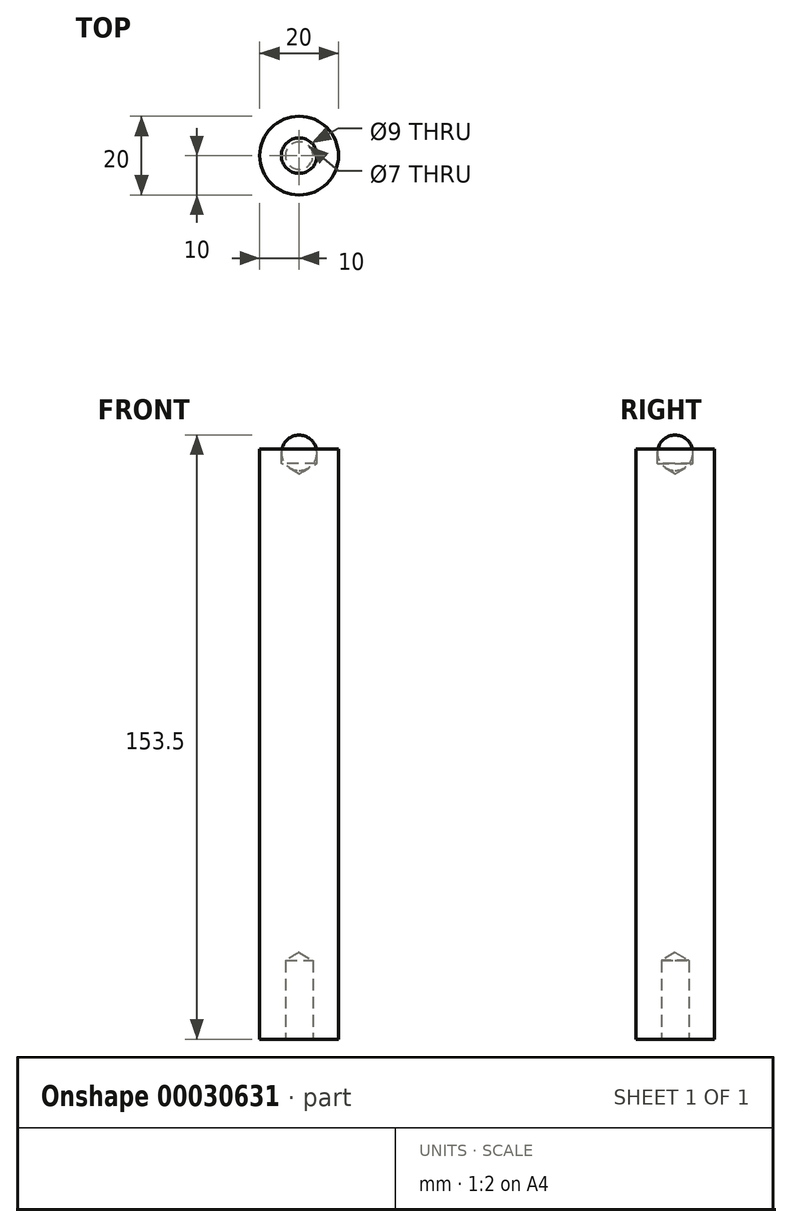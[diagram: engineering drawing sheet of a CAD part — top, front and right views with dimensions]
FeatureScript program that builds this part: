
annotation { "Feature Type Name" : "Feature", "Feature Type Description" : "" }
export const myFeature = defineFeature(function(context is Context, id is Id, definition is map)
    precondition{}
    {
        {
            var Q0;
            Q0=qCreatedBy(makeId("Front.planeOp"),FACE);
            var sketch = newSketch(context, id + "F0", { "sketchPlane" : qUnion([Q0])});
            skLineSegment(sketch, "E0.0", {"start": v(-10, 150) * mm, "end": v(-10, 0) * mm});
            skLineSegment(sketch, "E1", {"start": v(-10, 0) * mm, "end": v(0, 0) * mm});
            skLineSegment(sketch, "E2.0", {"start": v(-10, 150) * mm, "end": v(0, 150) * mm});
            skPoint(sketch, "E3.orphan", {"position": v(0, 44.07) * mm});
            skLineSegment(sketch, "E4", {"start": v(0, 150) * mm, "end": v(0, 0) * mm});
            skLineSegment(sketch, "E5", {"start": v(0, 150) * mm, "end": v(0, -57.25) * mm, "construction": true});
            skSolve(sketch);
        }
        {
            var Q0;
            Q0=makeQuery(id+"F0.imprint","IMPRINT",FACE,{"disambiguationData":[TD([[makeQuery(id+"F0.imprint","IMPRINT",EDGE,{"derivedFrom":sQuery(id+"F0.wireOp",EDGE,"E0.0")}),1.0]])]});
            var Q1;
            Q1=sQuery(id+"F0.wireOp",EDGE,"E5");
            revolve(context, id + "F1", {"entities" : qUnion([Q0]), "axis" : qUnion([Q1]), "revolveType" : RevolveType.FULL});
        }
        {
            var Q0;
            Q0=makeQuery(id+"F1.opRevolve","SWEPT_FACE",FACE,{"disambiguationData":[OSD([sQuery(id+"F0.wireOp",EDGE,"E2.0")])]});
            var sketch = newSketch(context, id + "F2", { "sketchPlane" : qUnion([Q0])});
            skCircle(sketch, "E6.0", {"center": v(0, 0) * mm, "radius": 10 * mm});
            skSolve(sketch);
        }
        {
            var Q0;
            Q0=sQuery(id+"F2.wireOp",VERTEX,"E6.0.center");
            var Q1;
            Q1=makeQuery(id+"F1.opRevolve","SWEPT_BODY",BODY,{"disambiguationData":[OSD([sQuery(id+"F0.wireOp",EDGE,"E0.0"),sQuery(id+"F0.wireOp",EDGE,"E1"),sQuery(id+"F0.wireOp",EDGE,"E2.0"),sQuery(id+"F0.wireOp",EDGE,"E4")])]});
            hole(context, id + "F3", {"style" : HoleStyle.SIMPLE, "holeDiameter" : 9 * mm, "endStyle" : HoleEndStyle.BLIND, "holeDepth" : 3.7 * mm, "locations" : qUnion([Q0]), "scope" : qUnion([Q1])});
        }
        {
            var Q0;
            Q0=makeQuery(id+"F1.opRevolve","SWEPT_FACE",FACE,{"disambiguationData":[OSD([sQuery(id+"F0.wireOp",EDGE,"E1")])]});
            var sketch = newSketch(context, id + "F4", { "sketchPlane" : qUnion([Q0])});
            skCircle(sketch, "E7.0", {"center": v(0, 0) * mm, "radius": 10 * mm});
            skSolve(sketch);
        }
        {
            var Q0;
            Q0=sQuery(id+"F4.wireOp",VERTEX,"E7.0.center");
            var Q1;
            Q1=makeQuery(id+"F1.opRevolve","SWEPT_BODY",BODY,{"disambiguationData":[OSD([sQuery(id+"F0.wireOp",EDGE,"E0.0"),sQuery(id+"F0.wireOp",EDGE,"E1"),sQuery(id+"F0.wireOp",EDGE,"E2.0"),sQuery(id+"F0.wireOp",EDGE,"E4")])]});
            hole(context, id + "F5", {"style" : HoleStyle.SIMPLE, "holeDiameter" : 7 * mm, "endStyle" : HoleEndStyle.BLIND, "holeDepth" : 20 * mm, "locations" : qUnion([Q0]), "scope" : qUnion([Q1])});
        }
        {
            var Q0;
            Q0=qCreatedBy(makeId("Front.planeOp"),FACE);
            var sketch = newSketch(context, id + "F6", { "sketchPlane" : qUnion([Q0])});
            skLineSegment(sketch, "E8.0", {"start": v(-4.5, 146.3) * mm, "end": v(4.5, 146.3) * mm, "construction": true});
            skLineSegment(sketch, "E9", {"start": v(4.5, 150) * mm, "end": v(4.5, 146) * mm});
            skLineSegment(sketch, "E10", {"start": v(-4.5, 146) * mm, "end": v(-4.5, 150) * mm});
            skLineSegment(sketch, "E11.0", {"start": v(-4.5, 150) * mm, "end": v(4.5, 150) * mm, "construction": true});
            skLineSegment(sketch, "E12", {"start": v(0, 144.5) * mm, "end": v(0, 153.74) * mm, "construction": true});
            skLineSegment(sketch, "E13.0", {"start": v(-3.5, 149) * mm, "end": v(3.5, 149) * mm, "construction": true});
            skArc(sketch, "E14", {"start": v(0, 153.5) * mm, "mid": v(-4.5, 149) * mm, "end": v(0, 144.5) * mm});
            skPoint(sketch, "E15.orphan", {"position": v(0, 146.3) * mm});
            skLineSegment(sketch, "E16", {"start": v(0, 144.5) * mm, "end": v(0, 153.5) * mm});
            skSolve(sketch);
        }
        {
            var Q0;
            {var subQ0=sQuery(id+"F6.wireOp",EDGE,"E16");Q0=makeQuery(id+"F6.imprint","IMPRINT",FACE,{"disambiguationData":[TD([[makeQuery(id+"F6.imprint","IMPRINT",EDGE,{"derivedFrom":subQ0}),1.0]])]});}
            var Q1;
            Q1=sQuery(id+"F6.wireOp",EDGE,"E16");
            revolve(context, id + "F7", {"entities" : qUnion([Q0]), "axis" : qUnion([Q1]), "revolveType" : RevolveType.FULL});
        }
    });
